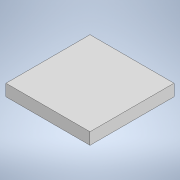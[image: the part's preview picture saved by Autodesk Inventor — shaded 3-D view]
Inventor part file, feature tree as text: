
AUTODESK INVENTOR PART (.ipt)
format: ipt  version: 2021.1 (Build 251245000, 245)  size: 144,896 bytes
history: native  units: mm
features: extrude x3, sketch x3, fillet x2
ambient origin geometry x8: Origin, YZ Plane, XZ Plane, XY Plane, X Axis, Y Axis, Z Axis, Center Point
bodies: Solid1 (feature_tree)
feature tree (8):
  extrude  "Extrusion1"  Depth=2.0mm TaperAngle=0.0deg
  extrude  "Extrusion2"  Depth=0.3mm
  extrude  "Extrusion3"  [1 undecoded]
  fillet  "Fillet1"  [1 undecoded]
  fillet  "Fillet2"  [1 undecoded]
  sketch  "Sketch1"  dims[d0=5.0mm d1=0.0mm d2=2.0mm d3=0.0mm]
  sketch  "Sketch2"  dims[d9=3.9mm d10=0.0mm d11=0.3mm]
  sketch  "Sketch3"  dims[d18=1.5mm]
note: 3 required parameter values undecoded (feature->parameter linkage not recoverable at this tier; creation-order binding heuristic only, values carry confidence <= 0.55)
